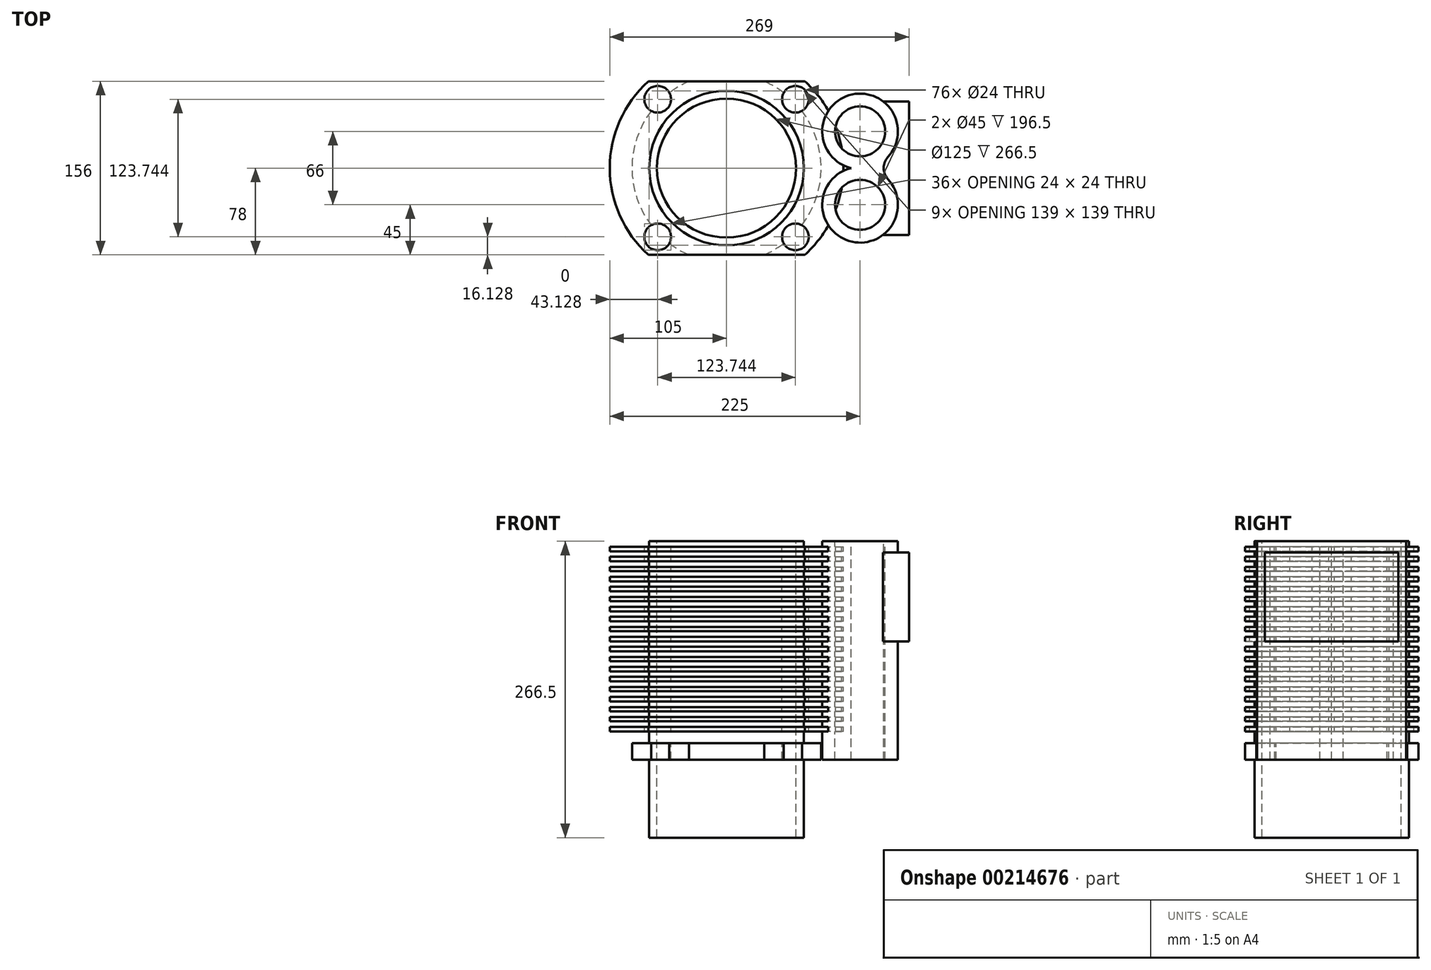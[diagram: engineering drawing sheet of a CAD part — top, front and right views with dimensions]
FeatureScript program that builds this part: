
annotation { "Feature Type Name" : "Feature", "Feature Type Description" : "" }
export const myFeature = defineFeature(function(context is Context, id is Id, definition is map)
    precondition{}
    {
        {
            var Q0;
            Q0=qCreatedBy(makeId("Top.planeOp"),FACE);
            var sketch = newSketch(context, id + "F0", { "sketchPlane" : qUnion([Q0])});
            skCircle(sketch, "E0", {"center": v(0, 0) * mm, "radius": 69.5 * mm});
            skCircle(sketch, "E1", {"center": v(0, 0) * mm, "radius": 62.5 * mm});
            skSolve(sketch);
        }
        {
            var Q0;
            Q0=makeQuery(id+"F0.imprint","IMPRINT",FACE,{"disambiguationData":[TD([[makeQuery(id+"F0.imprint","IMPRINT",EDGE,{"derivedFrom":sQuery(id+"F0.wireOp",EDGE,"E0")}),1.0]])]});
            extrude(context, id + "F1", {"entities" : qUnion([Q0]), "oppositeDirection" : true, "depth" : 266.5 * mm});
        }
        {
            var Q0;
            Q0=qCreatedBy(makeId("Front.planeOp"),FACE);
            var sketch = newSketch(context, id + "F2", { "sketchPlane" : qUnion([Q0])});
            skLineSegment(sketch, "E2", {"start": v(0, 0) * mm, "end": v(0, -266.5) * mm});
            skLineSegment(sketch, "E3", {"start": v(0, -196.5) * mm, "end": v(85, -196.5) * mm});
            skLineSegment(sketch, "E4", {"start": v(85, -196.5) * mm, "end": v(85, -181.5) * mm});
            skLineSegment(sketch, "E5", {"start": v(85, -181.5) * mm, "end": v(0, -181.5) * mm});
            skLineSegment(sketch, "E6", {"start": v(0, -5) * mm, "end": v(105, -5) * mm});
            skLineSegment(sketch, "E7", {"start": v(105, -5) * mm, "end": v(105, -9) * mm});
            skLineSegment(sketch, "E8", {"start": v(105, -9) * mm, "end": v(0, -9) * mm});
            skLineSegment(sketch, "E9.0.1.0", {"start": v(0, -14) * mm, "end": v(105, -14) * mm});
            skLineSegment(sketch, "E9.0.1.1", {"start": v(105, -18) * mm, "end": v(0, -18) * mm});
            skLineSegment(sketch, "E9.0.1.2", {"start": v(105, -14) * mm, "end": v(105, -18) * mm});
            skLineSegment(sketch, "E9.0.2.0", {"start": v(0, -23) * mm, "end": v(105, -23) * mm});
            skLineSegment(sketch, "E9.0.2.1", {"start": v(105, -27) * mm, "end": v(0, -27) * mm});
            skLineSegment(sketch, "E9.0.2.2", {"start": v(105, -23) * mm, "end": v(105, -27) * mm});
            skLineSegment(sketch, "E9.0.3.0", {"start": v(0, -32) * mm, "end": v(105, -32) * mm});
            skLineSegment(sketch, "E9.0.3.1", {"start": v(105, -36) * mm, "end": v(0, -36) * mm});
            skLineSegment(sketch, "E9.0.3.2", {"start": v(105, -32) * mm, "end": v(105, -36) * mm});
            skLineSegment(sketch, "E9.0.4.0", {"start": v(0, -41) * mm, "end": v(105, -41) * mm});
            skLineSegment(sketch, "E9.0.4.1", {"start": v(105, -45) * mm, "end": v(0, -45) * mm});
            skLineSegment(sketch, "E9.0.4.2", {"start": v(105, -41) * mm, "end": v(105, -45) * mm});
            skLineSegment(sketch, "E9.0.5.0", {"start": v(0, -50) * mm, "end": v(105, -50) * mm});
            skLineSegment(sketch, "E9.0.5.1", {"start": v(105, -54) * mm, "end": v(0, -54) * mm});
            skLineSegment(sketch, "E9.0.5.2", {"start": v(105, -50) * mm, "end": v(105, -54) * mm});
            skLineSegment(sketch, "E9.0.6.0", {"start": v(0, -59) * mm, "end": v(105, -59) * mm});
            skLineSegment(sketch, "E9.0.6.1", {"start": v(105, -63) * mm, "end": v(0, -63) * mm});
            skLineSegment(sketch, "E9.0.6.2", {"start": v(105, -59) * mm, "end": v(105, -63) * mm});
            skLineSegment(sketch, "E9.0.7.0", {"start": v(0, -68) * mm, "end": v(105, -68) * mm});
            skLineSegment(sketch, "E9.0.7.1", {"start": v(105, -72) * mm, "end": v(0, -72) * mm});
            skLineSegment(sketch, "E9.0.7.2", {"start": v(105, -68) * mm, "end": v(105, -72) * mm});
            skLineSegment(sketch, "E9.0.8.0", {"start": v(0, -77) * mm, "end": v(105, -77) * mm});
            skLineSegment(sketch, "E9.0.8.1", {"start": v(105, -81) * mm, "end": v(0, -81) * mm});
            skLineSegment(sketch, "E9.0.8.2", {"start": v(105, -77) * mm, "end": v(105, -81) * mm});
            skLineSegment(sketch, "E9.0.9.0", {"start": v(0, -86) * mm, "end": v(105, -86) * mm});
            skLineSegment(sketch, "E9.0.9.1", {"start": v(105, -90) * mm, "end": v(0, -90) * mm});
            skLineSegment(sketch, "E9.0.9.2", {"start": v(105, -86) * mm, "end": v(105, -90) * mm});
            skLineSegment(sketch, "E9.0.10.0", {"start": v(0, -95) * mm, "end": v(105, -95) * mm});
            skLineSegment(sketch, "E9.0.10.1", {"start": v(105, -99) * mm, "end": v(0, -99) * mm});
            skLineSegment(sketch, "E9.0.10.2", {"start": v(105, -95) * mm, "end": v(105, -99) * mm});
            skLineSegment(sketch, "E9.0.11.0", {"start": v(0, -104) * mm, "end": v(105, -104) * mm});
            skLineSegment(sketch, "E9.0.11.1", {"start": v(105, -108) * mm, "end": v(0, -108) * mm});
            skLineSegment(sketch, "E9.0.11.2", {"start": v(105, -104) * mm, "end": v(105, -108) * mm});
            skLineSegment(sketch, "E9.0.12.0", {"start": v(0, -113) * mm, "end": v(105, -113) * mm});
            skLineSegment(sketch, "E9.0.12.1", {"start": v(105, -117) * mm, "end": v(0, -117) * mm});
            skLineSegment(sketch, "E9.0.12.2", {"start": v(105, -113) * mm, "end": v(105, -117) * mm});
            skLineSegment(sketch, "E9.0.13.0", {"start": v(0, -122) * mm, "end": v(105, -122) * mm});
            skLineSegment(sketch, "E9.0.13.1", {"start": v(105, -126) * mm, "end": v(0, -126) * mm});
            skLineSegment(sketch, "E9.0.13.2", {"start": v(105, -122) * mm, "end": v(105, -126) * mm});
            skLineSegment(sketch, "E9.0.14.0", {"start": v(0, -131) * mm, "end": v(105, -131) * mm});
            skLineSegment(sketch, "E9.0.14.1", {"start": v(105, -135) * mm, "end": v(0, -135) * mm});
            skLineSegment(sketch, "E9.0.14.2", {"start": v(105, -131) * mm, "end": v(105, -135) * mm});
            skLineSegment(sketch, "E9.direction1", {"start": v(0, -5) * mm, "end": v(31, -5) * mm, "construction": true});
            skLineSegment(sketch, "E9.direction2", {"start": v(0, -5) * mm, "end": v(0, -14) * mm, "construction": true});
            skLineSegment(sketch, "E10.0.0.15", {"start": v(0, -140) * mm, "end": v(105, -140) * mm});
            skLineSegment(sketch, "E10.3.0.15", {"start": v(105, -144) * mm, "end": v(0, -144) * mm});
            skLineSegment(sketch, "E10.6.0.15", {"start": v(105, -140) * mm, "end": v(105, -144) * mm});
            skLineSegment(sketch, "E10.0.0.16", {"start": v(0, -149) * mm, "end": v(105, -149) * mm});
            skLineSegment(sketch, "E10.3.0.16", {"start": v(105, -153) * mm, "end": v(0, -153) * mm});
            skLineSegment(sketch, "E10.6.0.16", {"start": v(105, -149) * mm, "end": v(105, -153) * mm});
            skLineSegment(sketch, "E10.0.0.17", {"start": v(0, -158) * mm, "end": v(105, -158) * mm});
            skLineSegment(sketch, "E10.3.0.17", {"start": v(105, -162) * mm, "end": v(0, -162) * mm});
            skLineSegment(sketch, "E10.6.0.17", {"start": v(105, -158) * mm, "end": v(105, -162) * mm});
            skLineSegment(sketch, "E10.0.0.18", {"start": v(0, -167) * mm, "end": v(105, -167) * mm});
            skLineSegment(sketch, "E10.3.0.18", {"start": v(105, -171) * mm, "end": v(0, -171) * mm});
            skLineSegment(sketch, "E10.6.0.18", {"start": v(105, -167) * mm, "end": v(105, -171) * mm});
            skSolve(sketch);
        }
        {
            var Q0;
            {var subQ0=sQuery(id+"F2.wireOp",EDGE,"E3");Q0=makeQuery(id+"F2.imprint","IMPRINT",FACE,{"disambiguationData":[TD([[makeQuery(id+"F2.imprint","IMPRINT",EDGE,{"derivedFrom":subQ0}),1.0]])]});}
            var Q1;
            {var subQ0=sQuery(id+"F2.wireOp",EDGE,"E10.0.0.18");Q1=makeQuery(id+"F2.imprint","IMPRINT",FACE,{"disambiguationData":[TD([[makeQuery(id+"F2.imprint","IMPRINT",EDGE,{"derivedFrom":subQ0}),-1.0]])]});}
            var Q2;
            {var subQ0=sQuery(id+"F2.wireOp",EDGE,"E10.0.0.17");Q2=makeQuery(id+"F2.imprint","IMPRINT",FACE,{"disambiguationData":[TD([[makeQuery(id+"F2.imprint","IMPRINT",EDGE,{"derivedFrom":subQ0}),-1.0]])]});}
            var Q3;
            {var subQ0=sQuery(id+"F2.wireOp",EDGE,"E10.0.0.16");Q3=makeQuery(id+"F2.imprint","IMPRINT",FACE,{"disambiguationData":[TD([[makeQuery(id+"F2.imprint","IMPRINT",EDGE,{"derivedFrom":subQ0}),-1.0]])]});}
            var Q4;
            {var subQ0=sQuery(id+"F2.wireOp",EDGE,"E10.0.0.15");Q4=makeQuery(id+"F2.imprint","IMPRINT",FACE,{"disambiguationData":[TD([[makeQuery(id+"F2.imprint","IMPRINT",EDGE,{"derivedFrom":subQ0}),-1.0]])]});}
            var Q5;
            {var subQ0=sQuery(id+"F2.wireOp",EDGE,"E9.0.14.0");Q5=makeQuery(id+"F2.imprint","IMPRINT",FACE,{"disambiguationData":[TD([[makeQuery(id+"F2.imprint","IMPRINT",EDGE,{"derivedFrom":subQ0}),-1.0]])]});}
            var Q6;
            {var subQ0=sQuery(id+"F2.wireOp",EDGE,"E9.0.13.0");Q6=makeQuery(id+"F2.imprint","IMPRINT",FACE,{"disambiguationData":[TD([[makeQuery(id+"F2.imprint","IMPRINT",EDGE,{"derivedFrom":subQ0}),-1.0]])]});}
            var Q7;
            {var subQ0=sQuery(id+"F2.wireOp",EDGE,"E9.0.12.0");Q7=makeQuery(id+"F2.imprint","IMPRINT",FACE,{"disambiguationData":[TD([[makeQuery(id+"F2.imprint","IMPRINT",EDGE,{"derivedFrom":subQ0}),-1.0]])]});}
            var Q8;
            {var subQ0=sQuery(id+"F2.wireOp",EDGE,"E9.0.11.0");Q8=makeQuery(id+"F2.imprint","IMPRINT",FACE,{"disambiguationData":[TD([[makeQuery(id+"F2.imprint","IMPRINT",EDGE,{"derivedFrom":subQ0}),-1.0]])]});}
            var Q9;
            {var subQ0=sQuery(id+"F2.wireOp",EDGE,"E9.0.10.0");Q9=makeQuery(id+"F2.imprint","IMPRINT",FACE,{"disambiguationData":[TD([[makeQuery(id+"F2.imprint","IMPRINT",EDGE,{"derivedFrom":subQ0}),-1.0]])]});}
            var Q10;
            {var subQ0=sQuery(id+"F2.wireOp",EDGE,"E9.0.9.0");Q10=makeQuery(id+"F2.imprint","IMPRINT",FACE,{"disambiguationData":[TD([[makeQuery(id+"F2.imprint","IMPRINT",EDGE,{"derivedFrom":subQ0}),-1.0]])]});}
            var Q11;
            {var subQ0=sQuery(id+"F2.wireOp",EDGE,"E9.0.8.0");Q11=makeQuery(id+"F2.imprint","IMPRINT",FACE,{"disambiguationData":[TD([[makeQuery(id+"F2.imprint","IMPRINT",EDGE,{"derivedFrom":subQ0}),-1.0]])]});}
            var Q12;
            {var subQ0=sQuery(id+"F2.wireOp",EDGE,"E9.0.7.0");Q12=makeQuery(id+"F2.imprint","IMPRINT",FACE,{"disambiguationData":[TD([[makeQuery(id+"F2.imprint","IMPRINT",EDGE,{"derivedFrom":subQ0}),-1.0]])]});}
            var Q13;
            {var subQ0=sQuery(id+"F2.wireOp",EDGE,"E9.0.6.0");Q13=makeQuery(id+"F2.imprint","IMPRINT",FACE,{"disambiguationData":[TD([[makeQuery(id+"F2.imprint","IMPRINT",EDGE,{"derivedFrom":subQ0}),-1.0]])]});}
            var Q14;
            {var subQ0=sQuery(id+"F2.wireOp",EDGE,"E9.0.5.0");Q14=makeQuery(id+"F2.imprint","IMPRINT",FACE,{"disambiguationData":[TD([[makeQuery(id+"F2.imprint","IMPRINT",EDGE,{"derivedFrom":subQ0}),-1.0]])]});}
            var Q15;
            {var subQ0=sQuery(id+"F2.wireOp",EDGE,"E9.0.4.0");Q15=makeQuery(id+"F2.imprint","IMPRINT",FACE,{"disambiguationData":[TD([[makeQuery(id+"F2.imprint","IMPRINT",EDGE,{"derivedFrom":subQ0}),-1.0]])]});}
            var Q16;
            {var subQ0=sQuery(id+"F2.wireOp",EDGE,"E9.0.3.0");Q16=makeQuery(id+"F2.imprint","IMPRINT",FACE,{"disambiguationData":[TD([[makeQuery(id+"F2.imprint","IMPRINT",EDGE,{"derivedFrom":subQ0}),-1.0]])]});}
            var Q17;
            {var subQ0=sQuery(id+"F2.wireOp",EDGE,"E9.0.2.0");Q17=makeQuery(id+"F2.imprint","IMPRINT",FACE,{"disambiguationData":[TD([[makeQuery(id+"F2.imprint","IMPRINT",EDGE,{"derivedFrom":subQ0}),-1.0]])]});}
            var Q18;
            {var subQ0=sQuery(id+"F2.wireOp",EDGE,"E9.0.1.0");Q18=makeQuery(id+"F2.imprint","IMPRINT",FACE,{"disambiguationData":[TD([[makeQuery(id+"F2.imprint","IMPRINT",EDGE,{"derivedFrom":subQ0}),-1.0]])]});}
            var Q19;
            {var subQ0=sQuery(id+"F2.wireOp",EDGE,"E6");Q19=makeQuery(id+"F2.imprint","IMPRINT",FACE,{"disambiguationData":[TD([[makeQuery(id+"F2.imprint","IMPRINT",EDGE,{"derivedFrom":subQ0}),-1.0]])]});}
            var Q20;
            Q20=sQuery(id+"F2.wireOp",EDGE,"E2");
            revolve(context, id + "F3", {"operationType" : NewBodyOperationType.ADD, "entities" : qUnion([Q0, Q1, Q2, Q3, Q4, Q5, Q6, Q7, Q8, Q9, Q10, Q11, Q12, Q13, Q14, Q15, Q16, Q17, Q18, Q19]), "axis" : qUnion([Q20]), "revolveType" : RevolveType.FULL});
        }
        {
            var Q0;
            Q0=makeQuery(id+"F0.imprint","IMPRINT",FACE,{"disambiguationData":[TD([[makeQuery(id+"F0.imprint","IMPRINT",EDGE,{"derivedFrom":sQuery(id+"F0.wireOp",EDGE,"E1")}),1.0]])]});
            var Q1;
            Q1=sQuery(id+"F0.wireOp",EDGE,"E1");
            extrude(context, id + "F4", {"entities" : qUnion([Q0]), "operationType" : NewBodyOperationType.REMOVE, "surfaceEntities" : qUnion([Q1]), "oppositeDirection" : true, "depth" : 300 * mm});
        }
        {
            var Q0;
            Q0=qCreatedBy(makeId("Top.planeOp"),FACE);
            cPlane(context, id + "F5", {"entities" : qUnion([Q0]), "cplaneType" : CPlaneType.OFFSET, "offset" : 25 * mm, "width" : 150 * mm, "height" : 150 * mm});
        }
        {
            var Q0;
            Q0=qCreatedBy(id+"F5.planeOp",FACE);
            var sketch = newSketch(context, id + "F6", { "sketchPlane" : qUnion([Q0])});
            skLineSegment(sketch, "E11.bottom", {"start": v(125, 78) * mm, "end": v(-125, 78) * mm});
            skLineSegment(sketch, "E11.top", {"start": v(125, -78) * mm, "end": v(-125, -78) * mm});
            skLineSegment(sketch, "E11.left", {"start": v(125, 78) * mm, "end": v(125, -78) * mm});
            skLineSegment(sketch, "E11.right", {"start": v(-125, 78) * mm, "end": v(-125, -78) * mm});
            skLineSegment(sketch, "E12", {"start": v(0, 0) * mm, "end": v(-30.4, 0) * mm});
            skLineSegment(sketch, "E13.bottom", {"start": v(169.14, 132.13) * mm, "end": v(-146.14, 132.13) * mm});
            skLineSegment(sketch, "E13.top", {"start": v(169.14, -135.37) * mm, "end": v(-146.14, -135.37) * mm});
            skLineSegment(sketch, "E13.left", {"start": v(169.14, 132.13) * mm, "end": v(169.14, -135.37) * mm});
            skLineSegment(sketch, "E13.right", {"start": v(-146.14, 132.13) * mm, "end": v(-146.14, -135.37) * mm});
            skSolve(sketch);
        }
        {
            var Q0;
            Q0=makeQuery(id+"F6.imprint","IMPRINT",FACE,{"disambiguationData":[TD([[makeQuery(id+"F6.imprint","IMPRINT",EDGE,{"derivedFrom":sQuery(id+"F6.wireOp",EDGE,"E11.bottom")}),-1.0]])]});
            extrude(context, id + "F7", {"entities" : qUnion([Q0]), "operationType" : NewBodyOperationType.REMOVE, "oppositeDirection" : true, "depth" : 250 * mm});
        }
        {
            var Q0;
            Q0=qCreatedBy(id+"F5.planeOp",FACE);
            var sketch = newSketch(context, id + "F8", { "sketchPlane" : qUnion([Q0])});
            skCircle(sketch, "E14", {"center": v(0, 0) * mm, "radius": 87.5 * mm});
            skCircle(sketch, "E15", {"center": v(-87.5, 0) * mm, "radius": 12 * mm});
            skCircle(sketch, "E16.1.0", {"center": v(-61.87, -61.87) * mm, "radius": 12 * mm});
            skCircle(sketch, "E16.2.0", {"center": v(0, -87.5) * mm, "radius": 12 * mm});
            skCircle(sketch, "E16.3.0", {"center": v(61.87, -61.87) * mm, "radius": 12 * mm});
            skCircle(sketch, "E16.4.0", {"center": v(87.5, 0) * mm, "radius": 12 * mm});
            skCircle(sketch, "E16.5.0", {"center": v(61.87, 61.87) * mm, "radius": 12 * mm});
            skCircle(sketch, "E16.6.0", {"center": v(0, 87.5) * mm, "radius": 12 * mm});
            skCircle(sketch, "E16.7.0", {"center": v(-61.87, 61.87) * mm, "radius": 12 * mm});
            skSolve(sketch);
        }
        {
            var Q0;
            {var subQ0=sQuery(id+"F8.wireOp",EDGE,"E16.3.0");var subQ1=sQuery(id+"F8.wireOp",EDGE,"E14");var subQ2=makeQuery(id+"F8.imprint","INTERSECT",VERTEX,{"disambiguationData":[OD(0.0)],"derivedFrom":[subQ1,subQ0]});Q0=makeQuery(id+"F8.imprint","IMPRINT",FACE,{"disambiguationData":[TD([[makeQuery(id+"F8.imprint","IMPRINT",EDGE,{"disambiguationData":[TD([[subQ2,-1.0]])],"derivedFrom":subQ1}),-1.0]])]});}
            var Q1;
            {var subQ0=sQuery(id+"F8.wireOp",EDGE,"E16.3.0");var subQ1=sQuery(id+"F8.wireOp",EDGE,"E14");var subQ2=makeQuery(id+"F8.imprint","INTERSECT",VERTEX,{"disambiguationData":[OD(0.0)],"derivedFrom":[subQ1,subQ0]});Q1=makeQuery(id+"F8.imprint","IMPRINT",FACE,{"disambiguationData":[TD([[makeQuery(id+"F8.imprint","IMPRINT",EDGE,{"disambiguationData":[TD([[subQ2,-1.0]])],"derivedFrom":subQ1}),1.0]])]});}
            var Q2;
            {var subQ0=sQuery(id+"F8.wireOp",EDGE,"E16.1.0");var subQ1=sQuery(id+"F8.wireOp",EDGE,"E14");var subQ2=makeQuery(id+"F8.imprint","INTERSECT",VERTEX,{"disambiguationData":[OD(0.0)],"derivedFrom":[subQ1,subQ0]});Q2=makeQuery(id+"F8.imprint","IMPRINT",FACE,{"disambiguationData":[TD([[makeQuery(id+"F8.imprint","IMPRINT",EDGE,{"disambiguationData":[TD([[subQ2,-1.0]])],"derivedFrom":subQ1}),-1.0]])]});}
            var Q3;
            {var subQ0=sQuery(id+"F8.wireOp",EDGE,"E16.1.0");var subQ1=sQuery(id+"F8.wireOp",EDGE,"E14");var subQ2=makeQuery(id+"F8.imprint","INTERSECT",VERTEX,{"disambiguationData":[OD(0.0)],"derivedFrom":[subQ1,subQ0]});Q3=makeQuery(id+"F8.imprint","IMPRINT",FACE,{"disambiguationData":[TD([[makeQuery(id+"F8.imprint","IMPRINT",EDGE,{"disambiguationData":[TD([[subQ2,-1.0]])],"derivedFrom":subQ1}),1.0]])]});}
            var Q4;
            {var subQ0=sQuery(id+"F8.wireOp",EDGE,"E16.7.0");var subQ1=sQuery(id+"F8.wireOp",EDGE,"E14");var subQ2=makeQuery(id+"F8.imprint","INTERSECT",VERTEX,{"disambiguationData":[OD(0.0)],"derivedFrom":[subQ1,subQ0]});Q4=makeQuery(id+"F8.imprint","IMPRINT",FACE,{"disambiguationData":[TD([[makeQuery(id+"F8.imprint","IMPRINT",EDGE,{"disambiguationData":[TD([[subQ2,-1.0]])],"derivedFrom":subQ1}),-1.0]])]});}
            var Q5;
            {var subQ0=sQuery(id+"F8.wireOp",EDGE,"E16.7.0");var subQ1=sQuery(id+"F8.wireOp",EDGE,"E14");var subQ2=makeQuery(id+"F8.imprint","INTERSECT",VERTEX,{"disambiguationData":[OD(0.0)],"derivedFrom":[subQ1,subQ0]});Q5=makeQuery(id+"F8.imprint","IMPRINT",FACE,{"disambiguationData":[TD([[makeQuery(id+"F8.imprint","IMPRINT",EDGE,{"disambiguationData":[TD([[subQ2,-1.0]])],"derivedFrom":subQ1}),1.0]])]});}
            var Q6;
            {var subQ0=sQuery(id+"F8.wireOp",EDGE,"E16.5.0");var subQ1=sQuery(id+"F8.wireOp",EDGE,"E14");var subQ2=makeQuery(id+"F8.imprint","INTERSECT",VERTEX,{"disambiguationData":[OD(0.0)],"derivedFrom":[subQ1,subQ0]});Q6=makeQuery(id+"F8.imprint","IMPRINT",FACE,{"disambiguationData":[TD([[makeQuery(id+"F8.imprint","IMPRINT",EDGE,{"disambiguationData":[TD([[subQ2,-1.0]])],"derivedFrom":subQ1}),-1.0]])]});}
            var Q7;
            {var subQ0=sQuery(id+"F8.wireOp",EDGE,"E16.5.0");var subQ1=sQuery(id+"F8.wireOp",EDGE,"E14");var subQ2=makeQuery(id+"F8.imprint","INTERSECT",VERTEX,{"disambiguationData":[OD(0.0)],"derivedFrom":[subQ1,subQ0]});Q7=makeQuery(id+"F8.imprint","IMPRINT",FACE,{"disambiguationData":[TD([[makeQuery(id+"F8.imprint","IMPRINT",EDGE,{"disambiguationData":[TD([[subQ2,-1.0]])],"derivedFrom":subQ1}),1.0]])]});}
            extrude(context, id + "F9", {"entities" : qUnion([Q0, Q1, Q2, Q3, Q4, Q5, Q6, Q7]), "operationType" : NewBodyOperationType.REMOVE, "oppositeDirection" : true, "depth" : 250 * mm});
        }
        {
            var Q0;
            Q0=qCreatedBy(makeId("Top.planeOp"),FACE);
            var sketch = newSketch(context, id + "F10", { "sketchPlane" : qUnion([Q0])});
            skCircle(sketch, "E17", {"center": v(120, 33) * mm, "radius": 22.5 * mm});
            skLineSegment(sketch, "E18", {"start": v(0, 0) * mm, "end": v(24.07, 0) * mm});
            skCircle(sketch, "E19.MirrorC", {"center": v(120, -33) * mm, "radius": 22.5 * mm});
            skArc(sketch, "E20.MirrorC", {"start": v(145.13, -10.1) * mm, "mid": v(110.13, -65.54) * mm, "end": v(111.81, 0) * mm});
            skPoint(sketch, "E21.visualSharp", {"position": v(128.19, 0) * mm});
            skCircle(sketch, "E22", {"center": v(0, 0) * mm, "radius": 62.5 * mm});
            skPoint(sketch, "E23.start.orphan", {"position": v(24.07, 45) * mm});
            skArc(sketch, "E24.filletArc", {"start": v(145.13, 10.1) * mm, "mid": v(141.22, 0) * mm, "end": v(145.13, -10.1) * mm});
            skArc(sketch, "E25.converted", {"start": v(145.13, 10.1) * mm, "mid": v(110.13, 65.54) * mm, "end": v(111.81, 0) * mm});
            skCircle(sketch, "E26.converted", {"center": v(0, 0) * mm, "radius": 69.5 * mm});
            skSolve(sketch);
        }
        {
            var Q0;
            Q0=makeQuery(id+"F10.imprint","IMPRINT",FACE,{"disambiguationData":[TD([[makeQuery(id+"F10.imprint","IMPRINT",EDGE,{"derivedFrom":sQuery(id+"F10.wireOp",EDGE,"E17")}),-1.0]])]});
            extrude(context, id + "F11", {"entities" : qUnion([Q0]), "operationType" : NewBodyOperationType.ADD, "oppositeDirection" : true, "depth" : 196.5 * mm});
        }
        {
            var Q0;
            Q0=qCreatedBy(makeId("Right.planeOp"),FACE);
            cPlane(context, id + "F12", {"entities" : qUnion([Q0]), "cplaneType" : CPlaneType.OFFSET, "offset" : 164 * mm, "width" : 150 * mm, "height" : 150 * mm});
        }
        {
            var Q0;
            Q0=qCreatedBy(id+"F12.planeOp",FACE);
            var sketch = newSketch(context, id + "F13", { "sketchPlane" : qUnion([Q0])});
            skLineSegment(sketch, "E27.bottom", {"start": v(-60, -10) * mm, "end": v(60, -10) * mm});
            skLineSegment(sketch, "E27.top", {"start": v(-60, -90) * mm, "end": v(60, -90) * mm});
            skLineSegment(sketch, "E27.left", {"start": v(-60, -10) * mm, "end": v(-60, -90) * mm});
            skLineSegment(sketch, "E27.right", {"start": v(60, -10) * mm, "end": v(60, -90) * mm});
            skSolve(sketch);
        }
        {
            var Q0;
            Q0=makeQuery(id+"F13.imprint","IMPRINT",FACE,{"disambiguationData":[TD([[makeQuery(id+"F13.imprint","IMPRINT",EDGE,{"derivedFrom":sQuery(id+"F13.wireOp",EDGE,"E27.bottom")}),-1.0]])]});
            var Q1;
            Q1=makeQuery(id+"F11.opExtrude","SWEPT_FACE",FACE,{"disambiguationData":[OSD([sQuery(id+"F10.wireOp",EDGE,"E20.MirrorC")])]});
            var Q2;
            Q2=makeQuery(id+"F1.opExtrude","SWEPT_BODY",BODY,{"disambiguationData":[OSD([sQuery(id+"F0.wireOp",EDGE,"E0"),sQuery(id+"F0.wireOp",EDGE,"E1")])]});
            extrude(context, id + "F14", {"entities" : qUnion([Q0]), "operationType" : NewBodyOperationType.ADD, "endBound" : BoundingType.UP_TO_BODY, "oppositeDirection" : true, "endBoundEntityFace" : qUnion([Q1]), "endBoundEntityBody" : qUnion([Q2]), "depth" : 25 * mm});
        }
    });
